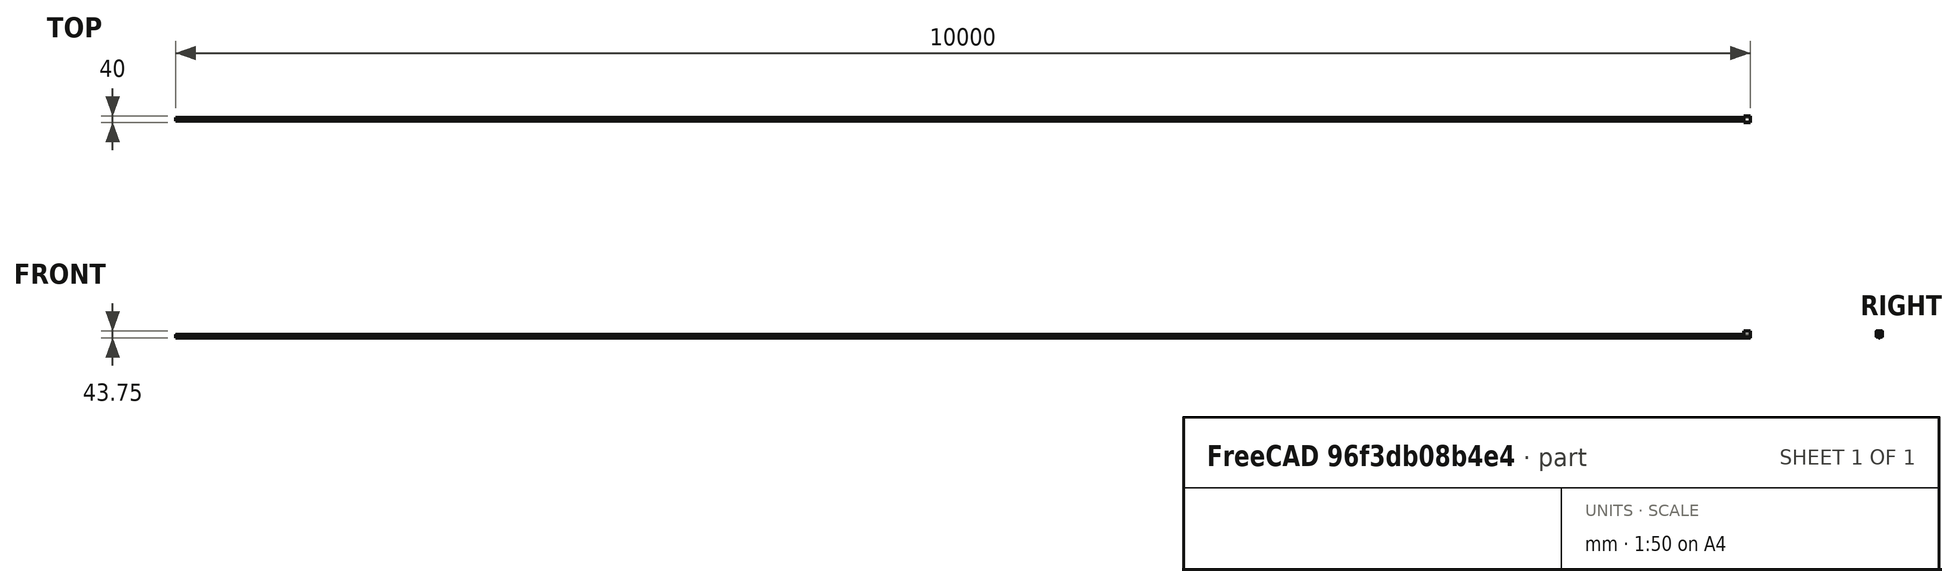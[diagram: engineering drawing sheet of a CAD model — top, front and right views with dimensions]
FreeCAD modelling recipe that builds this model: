
FCSTD DOCUMENT  (FreeCAD 0.16R)
Label: FlashLightClampHeadlamp
License: All rights reserved
LicenseURL: http://en.wikipedia.org/wiki/All_rights_reserved
objects: Sketcher::SketchObject×3, PartDesign::Fillet×3, PartDesign::Pocket×2, PartDesign::Pad×1, Mesh::Feature×1
note: 12 computed .brp shape members not serialized (recipe doc carries the construction recipe); baked Part::Feature solids carry a one-line shape summary decoded from their .brp

FEATURE [Sketcher::SketchObject] Sketch
  sketch-geometry (4):
    g0: LineSegment StartX=-20 StartY=20 StartZ=0 EndX=20 EndY=20 EndZ=0
    g1: LineSegment StartX=20 StartY=20 StartZ=0 EndX=20 EndY=-20 EndZ=0
    g2: LineSegment StartX=20 StartY=-20 StartZ=0 EndX=-20 EndY=-20 EndZ=0
    g3: LineSegment StartX=-20 StartY=-20 StartZ=0 EndX=-20 EndY=20 EndZ=0
  constraints (11):
    c: Coincident(g0,g1)
    c: Coincident(g1,g2)
    c: Coincident(g2,g3)
    c: Coincident(g3,g0)
    c: Horizontal(g0)
    c: Horizontal(g2)
    c: Vertical(g1)
    c: Vertical(g3)
    c: Symmetric(g0,g1,g-1)
    c: Distance(g0) = 40
    c: Distance(g1) = 40
FEATURE [PartDesign::Pad] Pad
  Length = 37
  Length2 = 100
  Sketch = -> Sketch
  Type = 0
FEATURE [Sketcher::SketchObject] Sketch001
  Placement = pos=(20,0,0) rot=(0.57735,0.57735,0.57735;2.0944rad)
  Support = -> Pad [Face2]
  sketch-geometry (1):
    g0: Circle CenterX=0 CenterY=4 CenterZ=0 NormalX=0 NormalY=0 NormalZ=1 Radius=10.75
  constraints (3):
    c: Radius(g0) = 10.75
    c: PointOnObject(g0,g-2)
    c: DistanceY(g0) = 4
FEATURE [PartDesign::Pocket] Pocket
  Length = 5
  Sketch = -> Sketch001
  Type = 1
FEATURE [Sketcher::SketchObject] Sketch002
  Placement = pos=(20,0,0) rot=(0.57735,0.57735,0.57735;2.0944rad)
  Support = -> Pocket [Face3]
  sketch-geometry (1):
    g0: Circle CenterX=0 CenterY=30 CenterZ=0 NormalX=0 NormalY=0 NormalZ=1 Radius=11.1
  constraints (3):
    c: Radius(g0) = 11.1
    c: PointOnObject(g0,g-2)
    c: DistanceY(g0) = 30
FEATURE [PartDesign::Pocket] Pocket001
  Length = 5
  Sketch = -> Sketch002
  Type = 1
FEATURE [PartDesign::Fillet] Fillet
  Base = -> Pocket001 [Edge29,Edge24]
  Radius = 2.5
FEATURE [PartDesign::Fillet] Fillet001
  Base = -> Fillet [Edge22,Edge31]
  Radius = 1
FEATURE [PartDesign::Fillet] Fillet002
  Base = -> Fillet001 [Edge39,Edge12,Edge34,Edge14,Edge10,Edge1,Edge5,Edge3,Edge21,Edge16]
  Radius = 2
FEATURE [Mesh::Feature] Mesh  label="Fillet002 (Meshed)"
